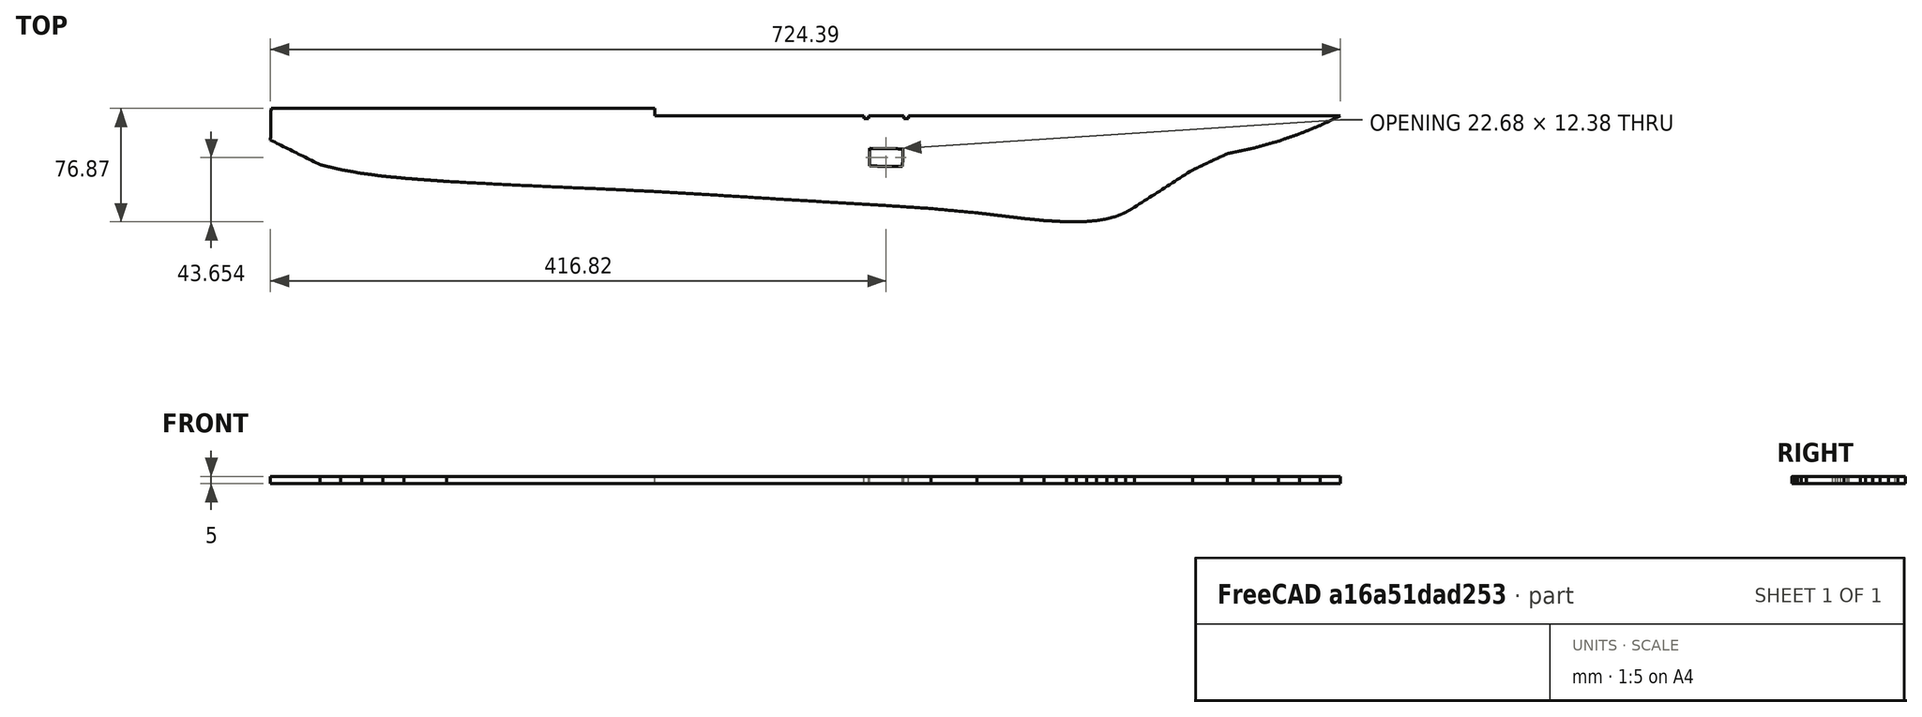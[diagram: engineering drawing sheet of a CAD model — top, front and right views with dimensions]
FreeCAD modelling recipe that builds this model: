
FCSTD DOCUMENT  (FreeCAD 0.19R)
Label: F-35_v2_parts_7
License: All rights reserved
LicenseURL: http://en.wikipedia.org/wiki/All_rights_reserved
objects: App::DocumentObjectGroup×2, PartDesign::CoordinateSystem×2, App::FeaturePython×1, Sketcher::SketchObject×1, PartDesign::Pad×1, PartDesign::Body×1, App::Part×1
note: 6 computed .brp shape members not serialized (recipe doc carries the construction recipe); baked Part::Feature solids carry a one-line shape summary decoded from their .brp

FEATURE [App::DocumentObjectGroup] Parts
FEATURE [PartDesign::CoordinateSystem] LCS_Origin
  AttacherType = Attacher::AttachEngine3D
  MapMode = 2
  Support = -> [X_Axis]
FEATURE [App::DocumentObjectGroup] Constraints
FEATURE [App::FeaturePython] Variables  # WARN: FeaturePython — macro-defined, semantics opaque (R4)
FEATURE [Sketcher::SketchObject] Sketch006
  FullyConstrained = false
  sketch-geometry (56):
    g0: BSplineCurve PolesCount=2 KnotsCount=2 Degree=1 IsPeriodic=0
    g1: BSplineCurve PolesCount=2 KnotsCount=2 Degree=1 IsPeriodic=0
    g2: BSplineCurve PolesCount=2 KnotsCount=2 Degree=1 IsPeriodic=0
    g3: BSplineCurve PolesCount=2 KnotsCount=2 Degree=1 IsPeriodic=0
    g4: BSplineCurve PolesCount=2 KnotsCount=2 Degree=1 IsPeriodic=0
    g5: BSplineCurve PolesCount=2 KnotsCount=2 Degree=1 IsPeriodic=0
    g6: BSplineCurve PolesCount=2 KnotsCount=2 Degree=1 IsPeriodic=0
    g7: BSplineCurve PolesCount=2 KnotsCount=2 Degree=1 IsPeriodic=0
    g8: BSplineCurve PolesCount=2 KnotsCount=2 Degree=1 IsPeriodic=0
    g9: BSplineCurve PolesCount=2 KnotsCount=2 Degree=1 IsPeriodic=0
    g10: BSplineCurve PolesCount=2 KnotsCount=2 Degree=1 IsPeriodic=0
    g11: BSplineCurve PolesCount=2 KnotsCount=2 Degree=1 IsPeriodic=0
    g12: BSplineCurve PolesCount=2 KnotsCount=2 Degree=1 IsPeriodic=0
    g13: BSplineCurve PolesCount=2 KnotsCount=2 Degree=1 IsPeriodic=0
    g14: BSplineCurve PolesCount=2 KnotsCount=2 Degree=1 IsPeriodic=0
    g15: BSplineCurve PolesCount=2 KnotsCount=2 Degree=1 IsPeriodic=0
    g16: BSplineCurve PolesCount=2 KnotsCount=2 Degree=1 IsPeriodic=0
    g17: BSplineCurve PolesCount=2 KnotsCount=2 Degree=1 IsPeriodic=0
    g18: BSplineCurve PolesCount=2 KnotsCount=2 Degree=1 IsPeriodic=0
    g19: BSplineCurve PolesCount=2 KnotsCount=2 Degree=1 IsPeriodic=0
    g20: BSplineCurve PolesCount=2 KnotsCount=2 Degree=1 IsPeriodic=0
    g21: BSplineCurve PolesCount=2 KnotsCount=2 Degree=1 IsPeriodic=0
    g22: BSplineCurve PolesCount=2 KnotsCount=2 Degree=1 IsPeriodic=0
    g23: BSplineCurve PolesCount=2 KnotsCount=2 Degree=1 IsPeriodic=0
    g24: BSplineCurve PolesCount=2 KnotsCount=2 Degree=1 IsPeriodic=0
    g25: BSplineCurve PolesCount=2 KnotsCount=2 Degree=1 IsPeriodic=0
    g26: BSplineCurve PolesCount=2 KnotsCount=2 Degree=1 IsPeriodic=0
    g27: BSplineCurve PolesCount=2 KnotsCount=2 Degree=1 IsPeriodic=0
    g28: BSplineCurve PolesCount=2 KnotsCount=2 Degree=1 IsPeriodic=0
    g29: BSplineCurve PolesCount=2 KnotsCount=2 Degree=1 IsPeriodic=0
    g30: BSplineCurve PolesCount=2 KnotsCount=2 Degree=1 IsPeriodic=0
    g31: BSplineCurve PolesCount=2 KnotsCount=2 Degree=1 IsPeriodic=0
    g32: BSplineCurve PolesCount=2 KnotsCount=2 Degree=1 IsPeriodic=0
    g33: BSplineCurve PolesCount=2 KnotsCount=2 Degree=1 IsPeriodic=0
    g34: BSplineCurve PolesCount=2 KnotsCount=2 Degree=1 IsPeriodic=0
    g35: BSplineCurve PolesCount=2 KnotsCount=2 Degree=1 IsPeriodic=0
    g36: BSplineCurve PolesCount=2 KnotsCount=2 Degree=1 IsPeriodic=0
    g37: BSplineCurve PolesCount=2 KnotsCount=2 Degree=1 IsPeriodic=0
    g38: BSplineCurve PolesCount=2 KnotsCount=2 Degree=1 IsPeriodic=0
    g39: BSplineCurve PolesCount=2 KnotsCount=2 Degree=1 IsPeriodic=0
    g40: BSplineCurve PolesCount=2 KnotsCount=2 Degree=1 IsPeriodic=0
    g41: BSplineCurve PolesCount=2 KnotsCount=2 Degree=1 IsPeriodic=0
    g42: BSplineCurve PolesCount=2 KnotsCount=2 Degree=1 IsPeriodic=0
    g43: BSplineCurve PolesCount=2 KnotsCount=2 Degree=1 IsPeriodic=0
    g44: BSplineCurve PolesCount=2 KnotsCount=2 Degree=1 IsPeriodic=0
    g45: BSplineCurve PolesCount=2 KnotsCount=2 Degree=1 IsPeriodic=0
    g46: BSplineCurve PolesCount=2 KnotsCount=2 Degree=1 IsPeriodic=0
    g47: BSplineCurve PolesCount=2 KnotsCount=2 Degree=1 IsPeriodic=0
    g48: BSplineCurve PolesCount=2 KnotsCount=2 Degree=1 IsPeriodic=0
    g49: BSplineCurve PolesCount=2 KnotsCount=2 Degree=1 IsPeriodic=0
    g50: BSplineCurve PolesCount=2 KnotsCount=2 Degree=1 IsPeriodic=0
    g51: BSplineCurve PolesCount=2 KnotsCount=2 Degree=1 IsPeriodic=0
    g52: BSplineCurve PolesCount=2 KnotsCount=2 Degree=1 IsPeriodic=0
    g53: BSplineCurve PolesCount=2 KnotsCount=2 Degree=1 IsPeriodic=0
    g54: BSplineCurve PolesCount=2 KnotsCount=2 Degree=1 IsPeriodic=0
    g55: BSplineCurve PolesCount=2 KnotsCount=2 Degree=1 IsPeriodic=0
  constraints (30):
    c: Coincident(g5,g6)
    c: Coincident(g6,g7)
    c: Coincident(g7,g8)
    c: Coincident(g8,g9)
    c: Coincident(g25,g26)
    c: Coincident(g26,g27)
    c: Coincident(g27,g28)
    c: Coincident(g28,g29)
    c: Coincident(g29,g30)
    c: Coincident(g30,g31)
    c: Coincident(g31,g32)
    c: Coincident(g32,g33)
    c: Coincident(g33,g34)
    c: Coincident(g34,g35)
    c: Coincident(g35,g36)
    c: Coincident(g36,g37)
    c: Coincident(g37,g38)
    c: Coincident(g38,g39)
    c: Coincident(g39,g40)
    c: Coincident(g40,g41)
    c: Coincident(g45,g46)
    c: Coincident(g46,g47)
    c: Coincident(g47,g48)
    c: Coincident(g48,g49)
    c: Coincident(g49,g50)
    c: Coincident(g50,g51)
    c: Coincident(g51,g52)
    c: Coincident(g52,g53)
    c: Coincident(g53,g54)
    c: Coincident(g54,g55)
FEATURE [PartDesign::Pad] Pad011
  Direction = (1,1,1)
  Length = 5
  Length2 = 100
  Profile = -> Sketch006
  Type = 0
FEATURE [PartDesign::Body] Body006  label="Part7"
  Group = -> [Sketch006,Pad011]
  Origin = -> Origin007
  Tip = -> Pad011
FEATURE [PartDesign::CoordinateSystem] LCS_1
  AttacherType = Attacher::AttachEngine3D
  MapMode = 7
  Placement = pos=(106.798,-421.762,0) rot=(0,1,0;3.14159rad)
  Support = -> [Pad011]
FEATURE [App::Part] Model
  Configuration = 0
  Group = -> [LCS_Origin,Constraints,Variables,Body006,LCS_1]
  Origin = -> Origin
  Type = Assembly4 Model
